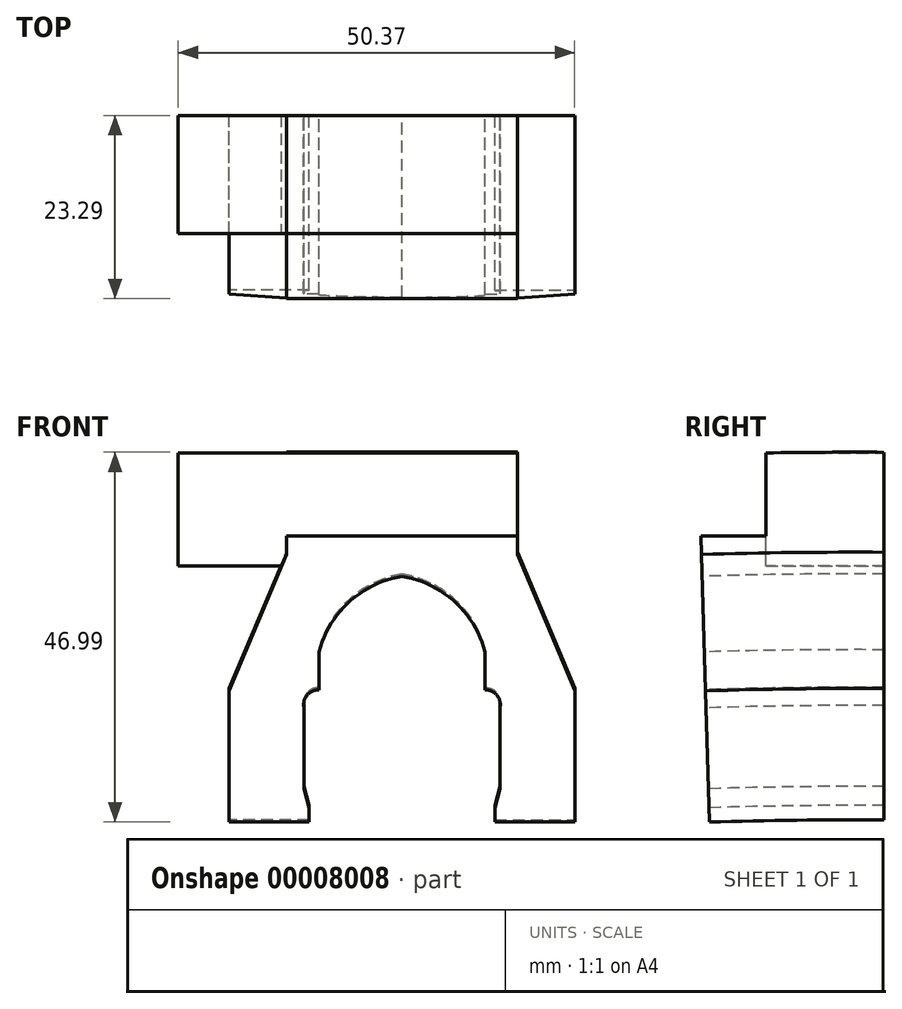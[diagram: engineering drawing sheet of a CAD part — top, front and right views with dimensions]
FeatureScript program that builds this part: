
annotation { "Feature Type Name" : "Feature", "Feature Type Description" : "" }
export const myFeature = defineFeature(function(context is Context, id is Id, definition is map)
    precondition{}
    {
        {
            var Q0;
            Q0=qCreatedBy(makeId("Front.planeOp"),FACE);
            var sketch = newSketch(context, id + "F0", { "sketchPlane" : qUnion([Q0])});
            skLineSegment(sketch, "E0", {"start": v(-11.78, 0) * mm, "end": v(-11.78, -1.82) * mm});
            skLineSegment(sketch, "E1", {"start": v(-11.78, -1.82) * mm, "end": v(-21.94, -1.82) * mm});
            skLineSegment(sketch, "E2", {"start": v(-21.94, -1.82) * mm, "end": v(-21.94, 14.86) * mm});
            skLineSegment(sketch, "E3", {"start": v(-11.78, 0) * mm, "end": v(-12.45, 2.41) * mm});
            skLineSegment(sketch, "E4", {"start": v(-12.45, 2.41) * mm, "end": v(-12.45, 12.7) * mm});
            skLineSegment(sketch, "E5", {"start": v(-10.54, 15) * mm, "end": v(-10.54, 19.8) * mm});
            skLineSegment(sketch, "E6", {"start": v(-14.64, 32.18) * mm, "end": v(-14.64, 44.88) * mm});
            skLineSegment(sketch, "E7", {"start": v(-14.64, 44.88) * mm, "end": v(0, 44.88) * mm});
            skLineSegment(sketch, "E8", {"start": v(0, 44.88) * mm, "end": v(0, 29.42) * mm});
            skArc(sketch, "E9", {"start": v(-10.54, 15) * mm, "mid": v(-12.05, 14.31) * mm, "end": v(-12.45, 12.7) * mm});
            skLineSegment(sketch, "E10", {"start": v(-21.94, 14.86) * mm, "end": v(-14.64, 32.18) * mm});
            skArc(sketch, "E11", {"start": v(0, 29.42) * mm, "mid": v(-6.7, 26.17) * mm, "end": v(-10.54, 19.8) * mm});
            skPoint(sketch, "E12.orphan", {"position": v(0, 19.8) * mm});
            skPoint(sketch, "E13.orphan", {"position": v(0, 28.42) * mm});
            skLineSegment(sketch, "E14", {"start": v(-11.32, 14.85) * mm, "end": v(8.61, 14.85) * mm, "construction": true});
            skLineSegment(sketch, "E15", {"start": v(-16.89, -607.45) * mm, "end": v(33.08, -607.45) * mm, "construction": true});
            skSolve(sketch);
        }
        {
            var Q0;
            Q0=makeQuery(id+"F0.imprint","IMPRINT",FACE,{"disambiguationData":[TD([[makeQuery(id+"F0.imprint","IMPRINT",EDGE,{"derivedFrom":sQuery(id+"F0.wireOp",EDGE,"E0")}),-1.0]])]});
            var Q1;
            Q1=sQuery(id+"F0.wireOp",EDGE,"E15");
            revolve(context, id + "F1", {"entities" : qUnion([Q0]), "axis" : qUnion([Q1]), "revolveType" : RevolveType.SYMMETRIC, "angle" : 3.5 * degree});
        }
        {
            var Q0;
            Q0=makeQuery(id+"F1.opRevolve","SWEPT_BODY",BODY,{"disambiguationData":[OSD([sQuery(id+"F0.wireOp",EDGE,"E0"),sQuery(id+"F0.wireOp",EDGE,"E1"),sQuery(id+"F0.wireOp",EDGE,"E2"),sQuery(id+"F0.wireOp",EDGE,"E3"),sQuery(id+"F0.wireOp",EDGE,"E4"),sQuery(id+"F0.wireOp",EDGE,"E5"),sQuery(id+"F0.wireOp",EDGE,"E6"),sQuery(id+"F0.wireOp",EDGE,"E7"),sQuery(id+"F0.wireOp",EDGE,"E8"),sQuery(id+"F0.wireOp",EDGE,"E9"),sQuery(id+"F0.wireOp",EDGE,"E10"),sQuery(id+"F0.wireOp",EDGE,"E11")])]});
            var Q1;
            Q1=qCreatedBy(makeId("Right.planeOp"),FACE);
            mirror(context, id + "F2", {"entities" : qUnion([Q0]), "mirrorPlane" : qUnion([Q1])});
        }
        {
            var Q0;
            Q0=qCreatedBy(makeId("Right.planeOp"),FACE);
            var sketch = newSketch(context, id + "F3", { "sketchPlane" : qUnion([Q0])});
            skLineSegment(sketch, "E16", {"start": v(0, 67.57) * mm, "end": v(0, 73.88) * mm});
            skLineSegment(sketch, "E17", {"start": v(0, 73.88) * mm, "end": v(-38.73, 73.88) * mm});
            skLineSegment(sketch, "E18", {"start": v(-38.73, 73.88) * mm, "end": v(-35.75, 29.88) * mm});
            skPoint(sketch, "E19.0.MirrorCS.start.orphan", {"position": v(38.73, 73.88) * mm});
            skPoint(sketch, "E20.0.MirrorCS.start.orphan", {"position": v(35.75, 29.88) * mm});
            skPoint(sketch, "E21.0.MirrorCS.start.orphan", {"position": v(4.2, 67.57) * mm});
            skLineSegment(sketch, "E22", {"start": v(-35.75, 29.88) * mm, "end": v(-25.68, 34.26) * mm});
            skLineSegment(sketch, "E23", {"start": v(-25.68, 34.26) * mm, "end": v(-11.3, 34.26) * mm});
            skLineSegment(sketch, "E24", {"start": v(-11.3, 34.26) * mm, "end": v(-11.3, 67.04) * mm});
            skPoint(sketch, "E25.start.orphan", {"position": v(-4.2, 67.57) * mm});
            skLineSegment(sketch, "E26", {"start": v(-11.3, 67.04) * mm, "end": v(0, 67.04) * mm});
            skLineSegment(sketch, "E27", {"start": v(0, 67.04) * mm, "end": v(0, 67.57) * mm});
            skLineSegment(sketch, "E28.0.MirrorCS", {"start": v(0, 73.88) * mm, "end": v(38.73, 73.88) * mm});
            skLineSegment(sketch, "E29.0.MirrorCS", {"start": v(38.73, 73.88) * mm, "end": v(35.75, 29.88) * mm});
            skLineSegment(sketch, "E30.0.MirrorCS", {"start": v(35.75, 29.88) * mm, "end": v(25.68, 34.26) * mm});
            skLineSegment(sketch, "E31.0.MirrorCS", {"start": v(25.68, 34.26) * mm, "end": v(11.3, 34.26) * mm});
            skLineSegment(sketch, "E32.0.MirrorCS", {"start": v(11.3, 34.26) * mm, "end": v(11.3, 67.04) * mm});
            skLineSegment(sketch, "E33.0.MirrorCS", {"start": v(11.3, 67.04) * mm, "end": v(0, 67.04) * mm});
            skSolve(sketch);
        }
        {
            var Q0;
            Q0=makeQuery(id+"F2.opPattern","COPY",BODY,{"derivedFrom":makeQuery(id+"F1.opRevolve","SWEPT_BODY",BODY,{"disambiguationData":[OSD([sQuery(id+"F0.wireOp",EDGE,"E0"),sQuery(id+"F0.wireOp",EDGE,"E1"),sQuery(id+"F0.wireOp",EDGE,"E2"),sQuery(id+"F0.wireOp",EDGE,"E3"),sQuery(id+"F0.wireOp",EDGE,"E4"),sQuery(id+"F0.wireOp",EDGE,"E5"),sQuery(id+"F0.wireOp",EDGE,"E6"),sQuery(id+"F0.wireOp",EDGE,"E7"),sQuery(id+"F0.wireOp",EDGE,"E8"),sQuery(id+"F0.wireOp",EDGE,"E9"),sQuery(id+"F0.wireOp",EDGE,"E10"),sQuery(id+"F0.wireOp",EDGE,"E11")])]}),"instanceName":"1"});
            var Q1;
            Q1=makeQuery(id+"F1.opRevolve","SWEPT_BODY",BODY,{"disambiguationData":[OSD([sQuery(id+"F0.wireOp",EDGE,"E0"),sQuery(id+"F0.wireOp",EDGE,"E1"),sQuery(id+"F0.wireOp",EDGE,"E2"),sQuery(id+"F0.wireOp",EDGE,"E3"),sQuery(id+"F0.wireOp",EDGE,"E4"),sQuery(id+"F0.wireOp",EDGE,"E5"),sQuery(id+"F0.wireOp",EDGE,"E6"),sQuery(id+"F0.wireOp",EDGE,"E7"),sQuery(id+"F0.wireOp",EDGE,"E8"),sQuery(id+"F0.wireOp",EDGE,"E9"),sQuery(id+"F0.wireOp",EDGE,"E10"),sQuery(id+"F0.wireOp",EDGE,"E11")])]});
            booleanBodies(context, id + "F4", {"operationType" : BooleanOperationType.UNION, "tools" : qUnion([Q0, Q1])});
        }
        {
            var Q0;
            Q0 = qSketchRegion(id + "F3", true);
            extrude(context, id + "F5", {"entities" : qUnion([Q0]), "operationType" : NewBodyOperationType.REMOVE, "endBound" : BoundingType.SYMMETRIC, "oppositeDirection" : true, "depth" : 50.8 * mm});
        }
        {
            var Q0;
            Q0=makeQuery(id+"F2.opPattern","COPY",FACE,{"derivedFrom":makeQuery(id+"F1.opRevolve","SWEPT_FACE",FACE,{"disambiguationData":[OSD([sQuery(id+"F0.wireOp",EDGE,"E6")])]}),"instanceName":"1"});
            var sketch = newSketch(context, id + "F6", { "sketchPlane" : qUnion([Q0])});
            skLineSegment(sketch, "E34.bottom", {"start": v(-11.3, 44.79) * mm, "end": v(11.3, 44.79) * mm});
            skLineSegment(sketch, "E34.top", {"start": v(-11.3, 30.44) * mm, "end": v(11.3, 30.44) * mm});
            skLineSegment(sketch, "E34.left", {"start": v(-11.3, 44.79) * mm, "end": v(-11.3, 30.44) * mm});
            skLineSegment(sketch, "E34.right", {"start": v(11.3, 44.79) * mm, "end": v(11.3, 30.44) * mm});
            skSolve(sketch);
        }
        {
            var Q0;
            Q0 = qSketchRegion(id + "F6", true);
            extrude(context, id + "F7", {"entities" : qUnion([Q0]), "operationType" : NewBodyOperationType.ADD, "oppositeDirection" : true, "depth" : 44.45 * mm});
        }
        {
            var Q0;
            Q0=makeQuery(id+"F7.boolean.opBoolean","MERGE",FACE,{"derivedFrom":[makeQuery(id+"F5.boolean.opBoolean","COPY",FACE,{"derivedFrom":makeQuery(id+"F5.opExtrude","SWEPT_FACE",FACE,{"disambiguationData":[OSD([sQuery(id+"F3.wireOp",EDGE,"E32.0.MirrorCS")])]})}),makeQuery(id+"F7.opExtrude","SWEPT_FACE",FACE,{"disambiguationData":[OSD([sQuery(id+"F6.wireOp",EDGE,"E34.right")])]})]});
            var sketch = newSketch(context, id + "F8", { "sketchPlane" : qUnion([Q0])});
            skLineSegment(sketch, "E35.bottom", {"start": v(29.8, 44.79) * mm, "end": v(84.3, 44.79) * mm});
            skLineSegment(sketch, "E35.top", {"start": v(29.8, 30.34) * mm, "end": v(84.3, 30.34) * mm});
            skLineSegment(sketch, "E35.left", {"start": v(29.8, 44.79) * mm, "end": v(29.8, 30.34) * mm});
            skLineSegment(sketch, "E35.right", {"start": v(84.3, 44.79) * mm, "end": v(84.3, 30.34) * mm});
            skSolve(sketch);
        }
        {
            var Q0;
            Q0 = qSketchRegion(id + "F8", true);
            extrude(context, id + "F9", {"entities" : qUnion([Q0]), "operationType" : NewBodyOperationType.ADD, "depth" : 25.4 * mm});
        }
        {
            var Q0;
            Q0=makeQuery(id+"F9.opExtrude","CAP_FACE",FACE,{"disambiguationData":[OSD([sQuery(id+"F8.wireOp",EDGE,"E35.bottom"),sQuery(id+"F8.wireOp",EDGE,"E35.top"),sQuery(id+"F8.wireOp",EDGE,"E35.left"),sQuery(id+"F8.wireOp",EDGE,"E35.right")])],"isStart":false});
            var sketch = newSketch(context, id + "F10", { "sketchPlane" : qUnion([Q0])});
            skLineSegment(sketch, "E36.bottom", {"start": v(-54.17, 59.58) * mm, "end": v(42.71, 59.58) * mm});
            skLineSegment(sketch, "E36.top", {"start": v(-54.17, -10.06) * mm, "end": v(42.71, -10.06) * mm});
            skLineSegment(sketch, "E36.left", {"start": v(-54.17, 59.58) * mm, "end": v(-54.17, -10.06) * mm});
            skLineSegment(sketch, "E36.right", {"start": v(42.71, 59.58) * mm, "end": v(42.71, -10.06) * mm});
            skSolve(sketch);
        }
        {
            var Q0;
            Q0 = qSketchRegion(id + "F10", true);
            extrude(context, id + "F11", {"entities" : qUnion([Q0]), "operationType" : NewBodyOperationType.REMOVE, "oppositeDirection" : true, "depth" : 33.02 * mm});
        }
        {
            var Q0;
            Q0=makeQuery(id+"F9.opExtrude","SWEPT_FACE",FACE,{"disambiguationData":[OSD([sQuery(id+"F8.wireOp",EDGE,"E35.right")])]});
            var sketch = newSketch(context, id + "F12", { "sketchPlane" : qUnion([Q0])});
            skLineSegment(sketch, "E37.bottom", {"start": v(-54.2, 60.61) * mm, "end": v(50.2, 60.61) * mm});
            skLineSegment(sketch, "E37.top", {"start": v(-54.2, 13.55) * mm, "end": v(50.2, 13.55) * mm});
            skLineSegment(sketch, "E37.left", {"start": v(-54.2, 60.61) * mm, "end": v(-54.2, 13.55) * mm});
            skLineSegment(sketch, "E37.right", {"start": v(50.2, 60.61) * mm, "end": v(50.2, 13.55) * mm});
            skSolve(sketch);
        }
        {
            var Q0;
            Q0 = qSketchRegion(id + "F12", true);
            extrude(context, id + "F13", {"entities" : qUnion([Q0]), "operationType" : NewBodyOperationType.REMOVE, "oppositeDirection" : true, "depth" : 55.88 * mm});
        }
    });
